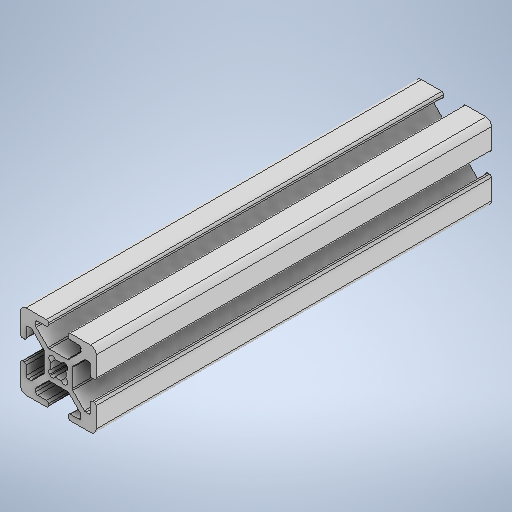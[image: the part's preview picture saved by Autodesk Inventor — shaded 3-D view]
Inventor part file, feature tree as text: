
AUTODESK INVENTOR PART (.ipt)
format: ipt  version: 2025 (Build 290162000, 162)  size: 375,296 bytes
history: native  units: mm
features: extrude x1, sketch x1
ambient origin geometry x8: Origin, YZ Plane, XZ Plane, XY Plane, X Axis, Y Axis, Z Axis, Center Point
bodies: Solid1 (feature_tree)
feature tree (2):
  extrude  "Extrusion1"  Depth=104.525mm
  sketch  "Sketch1"  dims[d0=104.525mm d1=0.0mm d2=1.0mm d3=1.0mm d4=1.0mm d5=0.15mm d6=0.25mm d7=0.375mm d8=14.3117mm d9=0.75mm d10=20.594885mm d11=0.0625mm d12=0.75mm d13=0.375mm]
